# Revit family: 318_e72811ac99cf4a90a71bde11d07fb8
name_source: partatom
category: Pipe Accessories
units: mm (PartAtom-declared; Revit-internal decimal feet)

## family parameters
Always vertical = Yes
Cut with Voids When Loaded = No
Part Type = Valve - Normal
Round Connector Dimension = Use Diameter
Shared = No
Work Plane-Based = No

## types (1)
- FAR-3874 11212200
    BP = 15 mm
    CAT0 = Yes
    CenSd_R3_6 = 23 mm
    D = 25 mm  [stored 0.082021 ft]
    Description = START 1"1/2 flanged joint manifold f-f, 1 port 1/2"f, 200 mm
    E = 29 mm  [stored 0.0951444 ft]
    H1 = 41 mm  [stored 0.134514 ft]
    H2 = 27 mm
    L1 = 159 mm  [stored 0.521654 ft]
    L2 = 41 mm  [stored 0.134514 ft]
    L3 = 10 mm  [stored 0.0328084 ft]
    L3__ve = -10 mm  [stored -0.0328084 ft]
    L4 = 139 mm
    L4__ve = -139 mm  [stored -0.456037 ft]
    L5 = 21 mm  [stored 0.0688976 ft]
    MP1 = 40 mm
    MP2 = 40 mm
    Manufacturer = FAR
    QmdConnectorList = 301;MP1;302;MP2;303;BP
    R1 = 20 mm  [stored 0.0656168 ft]
    R3 = 26 mm  [stored 0.0853018 ft]
    R4 = 22 mm  [stored 0.0721785 ft]
    R5 = 16 mm
    R6 = 18 mm
    R8 = 10 mm  [stored 0.0328084 ft]
    URL = www.far.eu
    W1 = 10 mm  [stored 0.0328084 ft]
    W3 = 48 mm
    W3__ve = -48 mm
    W4 = 4 mm  [stored 0.0131234 ft]
    W4__ve = -4 mm
    W5 = 13 mm
    W5__ve = -13 mm
    magiPartTypeId = 318
    magiProductCode = FAR-3874 11212200
    magiProductFamilyId = e72811ac99cf4a90a71bde11d07fb8
    magiProductId = e72811ac99cf4a90a71bde11d07fb8

note: [stored X ft] marks values corroborated as IEEE doubles in the binary element streams (Revit-internal decimal feet)

## geometry (parser evidence)
native form markers: Sweep x2
no freeform markers — native parametric forms only
